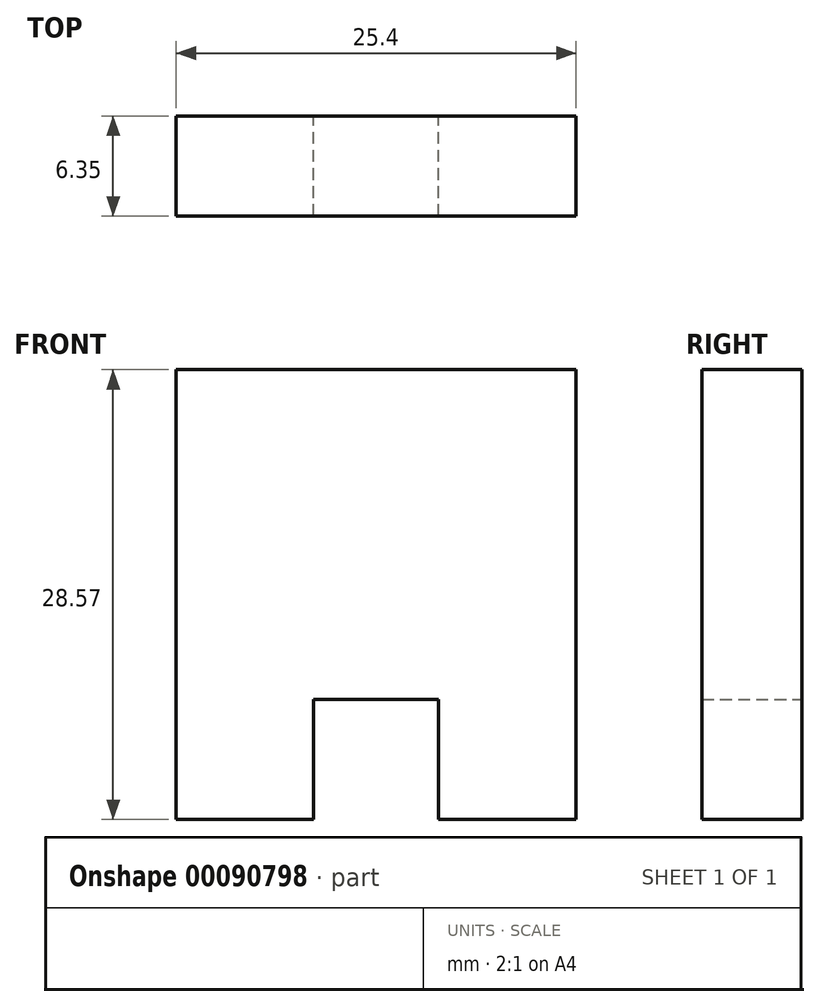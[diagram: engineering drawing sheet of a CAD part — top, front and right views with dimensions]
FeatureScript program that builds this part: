
annotation { "Feature Type Name" : "Feature", "Feature Type Description" : "" }
export const myFeature = defineFeature(function(context is Context, id is Id, definition is map)
    precondition{}
    {
        {
            var Q0;
            Q0=qCreatedBy(makeId("Front.planeOp"),FACE);
            var sketch = newSketch(context, id + "F0", { "sketchPlane" : qUnion([Q0])});
            skLineSegment(sketch, "E0.bottom", {"start": v(0, 0) * mm, "end": v(25.4, 0) * mm});
            skLineSegment(sketch, "E0.top", {"start": v(0, -28.58) * mm, "end": v(25.4, -28.58) * mm});
            skLineSegment(sketch, "E0.left", {"start": v(0, 0) * mm, "end": v(0, -28.58) * mm});
            skLineSegment(sketch, "E0.right", {"start": v(25.4, 0) * mm, "end": v(25.4, -28.58) * mm});
            skLineSegment(sketch, "E1.bottom", {"start": v(12.7, -28.58) * mm, "end": v(8.73, -28.58) * mm});
            skLineSegment(sketch, "E1.top", {"start": v(12.7, -20.96) * mm, "end": v(8.73, -20.96) * mm});
            skLineSegment(sketch, "E1.left", {"start": v(12.7, -28.58) * mm, "end": v(12.7, -20.96) * mm});
            skLineSegment(sketch, "E1.right", {"start": v(8.73, -28.58) * mm, "end": v(8.73, -20.96) * mm});
            skLineSegment(sketch, "E2.MirrorCS", {"start": v(12.7, -20.96) * mm, "end": v(16.67, -20.96) * mm});
            skLineSegment(sketch, "E3.MirrorCS", {"start": v(16.67, -28.58) * mm, "end": v(16.67, -20.96) * mm});
            skLineSegment(sketch, "E4.MirrorCS", {"start": v(12.7, -28.58) * mm, "end": v(16.67, -28.58) * mm});
            skSolve(sketch);
        }
        {
            var Q0;
            Q0=makeQuery(id+"F0.imprint","IMPRINT",FACE,{"disambiguationData":[TD([[makeQuery(id+"F0.imprint","IMPRINT",EDGE,{"derivedFrom":sQuery(id+"F0.wireOp",EDGE,"E0.bottom")}),-1.0]])]});
            extrude(context, id + "F1", {"entities" : qUnion([Q0]), "depth" : 6.35 * mm});
        }
    });
